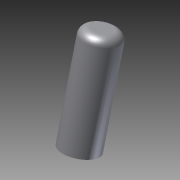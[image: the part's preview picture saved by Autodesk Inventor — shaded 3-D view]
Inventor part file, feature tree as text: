
AUTODESK INVENTOR PART (.ipt)
format: ipt  version: 2011 SP1 (Build 150282100, 282)  size: 87,040 bytes
history: native  units: in
note: dims shown in document units (in); Inventor stores cm internally (conversion verified against a paired STEP export)
features: other x7, revolve x1, sketch x1
ambient origin geometry x8: Origin, YZ Plane, XZ Plane, XY Plane, X Axis, Y Axis, Z Axis, Center Point
bodies: Solid1 (feature_tree)
feature tree (9):
  revolve  "Revolution1"  [1 undecoded]
  other  "to_body_XY"
  other  "to_body_YZ"
  other  "to_body_ZX"
  other  "to_body_X"
  other  "to_body_Y"
  other  "to_body_Z"
  other  "to_body_Center"
  sketch  "Sketch_1"  dims[d0=360.0deg]
note: 1 required parameter value undecoded (feature->parameter linkage not recoverable at this tier; creation-order binding heuristic only, values carry confidence <= 0.55)
